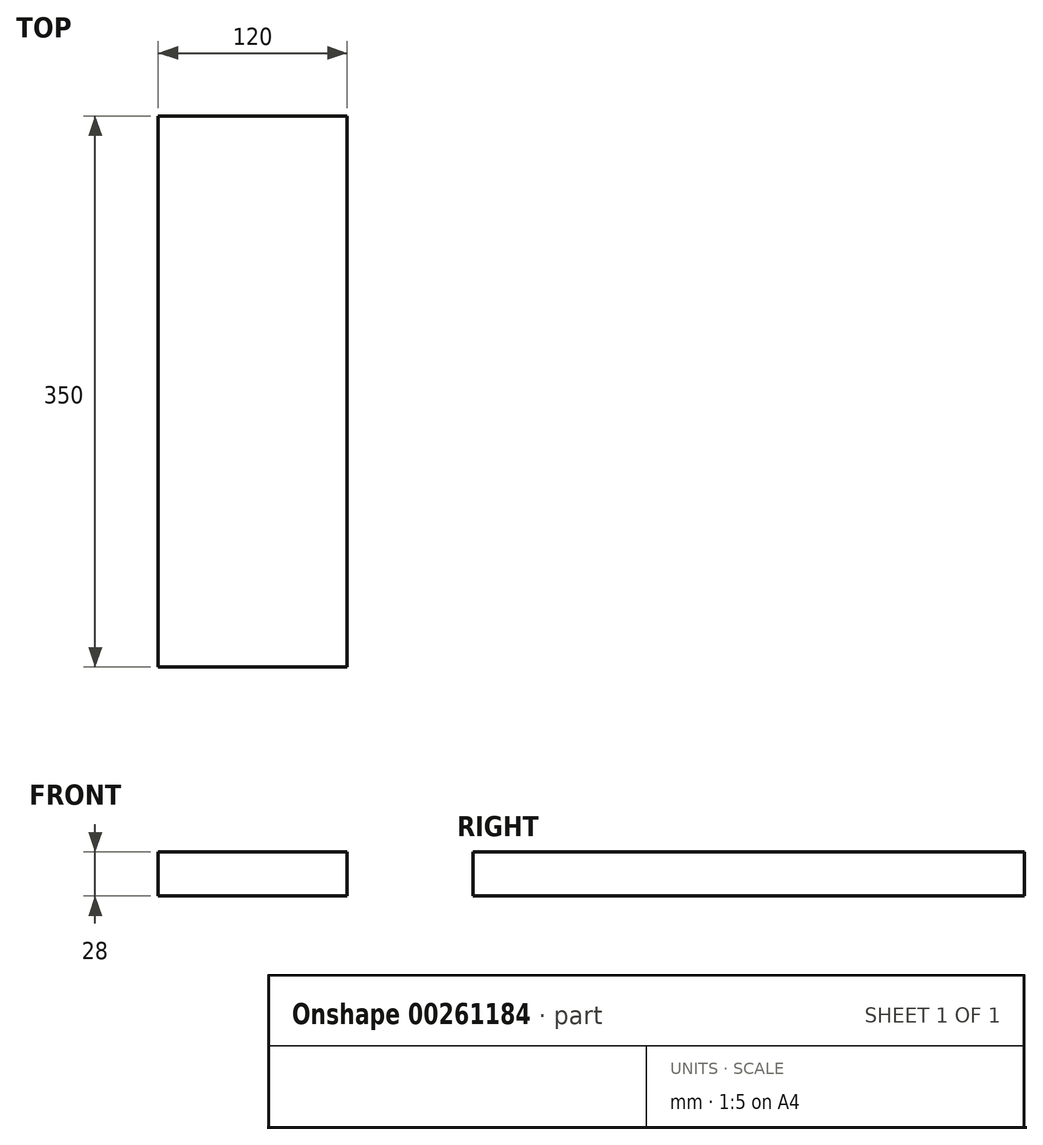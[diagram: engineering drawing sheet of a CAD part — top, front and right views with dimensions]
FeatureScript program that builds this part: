
annotation { "Feature Type Name" : "Feature", "Feature Type Description" : "" }
export const myFeature = defineFeature(function(context is Context, id is Id, definition is map)
    precondition{}
    {
        {
            var Q0;
            Q0=qCreatedBy(makeId("Front.planeOp"),FACE);
            var sketch = newSketch(context, id + "F0", { "sketchPlane" : qUnion([Q0])});
            skLineSegment(sketch, "E0.bottom", {"start": v(-60, -14) * mm, "end": v(60, -14) * mm});
            skLineSegment(sketch, "E0.top", {"start": v(-60, 14) * mm, "end": v(60, 14) * mm});
            skLineSegment(sketch, "E0.left", {"start": v(-60, -14) * mm, "end": v(-60, 14) * mm});
            skLineSegment(sketch, "E0.right", {"start": v(60, -14) * mm, "end": v(60, 14) * mm});
            skPoint(sketch, "E1", {"position": v(-60, 0) * mm});
            skPoint(sketch, "E2", {"position": v(0, 14) * mm});
            skSolve(sketch);
        }
        {
            var Q0;
            Q0 = qSketchRegion(id + "F0", true);
            extrude(context, id + "F1", {"entities" : qUnion([Q0]), "endBound" : BoundingType.SYMMETRIC, "depth" : 350 * mm});
        }
    });
